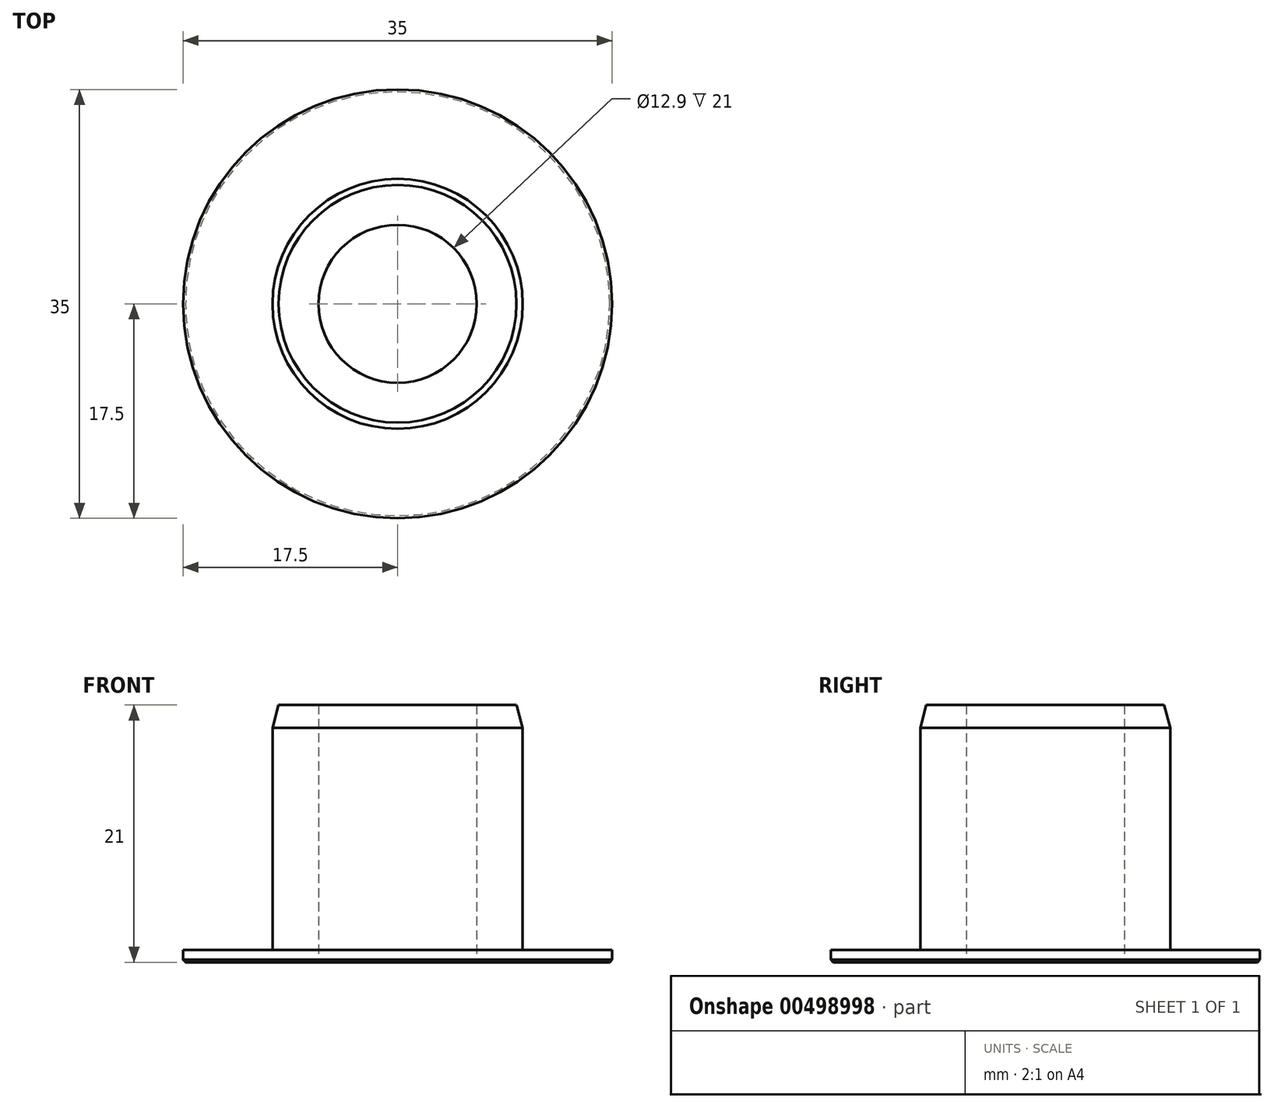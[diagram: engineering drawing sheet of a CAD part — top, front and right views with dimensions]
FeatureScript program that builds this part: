
annotation { "Feature Type Name" : "Feature", "Feature Type Description" : "" }
export const myFeature = defineFeature(function(context is Context, id is Id, definition is map)
    precondition{}
    {
        {
            assignVariable(context, id + "F0", {"name" : "Bohrung", "anyValue" : 0.6});
        }
        {
            var Q0;
            Q0=qCreatedBy(makeId("Top.planeOp"),FACE);
            var sketch = newSketch(context, id + "F1", { "sketchPlane" : qUnion([Q0])});
            skPoint(sketch, "E0", {"position": v(0, 0) * mm});
            skCircle(sketch, "E1", {"center": v(0, 0) * mm, "radius": 10.2 * mm});
            skSolve(sketch);
        }
        {
            var Q0;
            Q0=makeQuery(id+"F1.imprint","IMPRINT",FACE,{"disambiguationData":[TD([[makeQuery(id+"F1.imprint","IMPRINT",EDGE,{"derivedFrom":sQuery(id+"F1.wireOp",EDGE,"E1")}),1.0]])]});
            extrude(context, id + "F2", {"entities" : qUnion([Q0]), "depth" : 20 * mm});
        }
        {
            var Q0;
            Q0=makeQuery(id+"F2.opExtrude","CAP_FACE",FACE,{"disambiguationData":[OSD([sQuery(id+"F1.wireOp",EDGE,"E1")])],"isStart":true});
            var sketch = newSketch(context, id + "F3", { "sketchPlane" : qUnion([Q0])});
            skCircle(sketch, "E2", {"center": v(0, 0) * mm, "radius": 17.5 * mm});
            skSolve(sketch);
        }
        {
            var Q0;
            Q0 = qSketchRegion(id + "F3", true);
            extrude(context, id + "F4", {"entities" : qUnion([Q0]), "operationType" : NewBodyOperationType.ADD, "depth" : 1 * mm});
        }
        {
            var Q0;
            Q0=makeQuery(id+"F4.opExtrude","CAP_FACE",FACE,{"disambiguationData":[OSD([sQuery(id+"F3.wireOp",EDGE,"E2")])],"isStart":false});
            var sketch = newSketch(context, id + "F5", { "sketchPlane" : qUnion([Q0])});
            skPoint(sketch, "E3", {"position": v(0, 0) * mm});
            skSolve(sketch);
        }
        {
            var Q0;
            Q0=sQuery(id+"F5.wireOp",VERTEX,"E3");
            var Q1;
            Q1=makeQuery(id+"F2.opExtrude","SWEPT_BODY",BODY,{"disambiguationData":[OSD([sQuery(id+"F1.wireOp",EDGE,"E1")])]});
            hole(context, id + "F6", {"style" : HoleStyle.SIMPLE, "endStyle" : HoleEndStyle.THROUGH, "holeDiameter" : (12.3 + getVariable(context, 'Bohrung')) * mm, "isTappedThrough" : true, "tappedDepth" : 12 * mm, "tapClearance" : 3, "locations" : qUnion([Q0]), "scope" : qUnion([Q1])});
        }
        {
            var Q0;
            Q0=makeQuery(id+"F4.opExtrude","CAP_EDGE",EDGE,{"disambiguationData":[OSD([sQuery(id+"F3.wireOp",EDGE,"E2")])],"isStart":false});
            chamfer(context, id + "F7", {"entities" : qUnion([Q0]), "chamferType" : ChamferType.OFFSET_ANGLE, "width" : 0.2 * mm, "oppositeDirection" : false, "angle" : 45 * degree});
        }
        {
            var Q0;
            Q0=makeQuery(id+"F2.opExtrude","CAP_EDGE",EDGE,{"disambiguationData":[OSD([sQuery(id+"F1.wireOp",EDGE,"E1")])],"isStart":false});
            chamfer(context, id + "F8", {"entities" : qUnion([Q0]), "chamferType" : ChamferType.OFFSET_ANGLE, "width" : 0.5 * mm, "oppositeDirection" : false, "angle" : 75 * degree, "tangentPropagation" : true});
        }
    });
